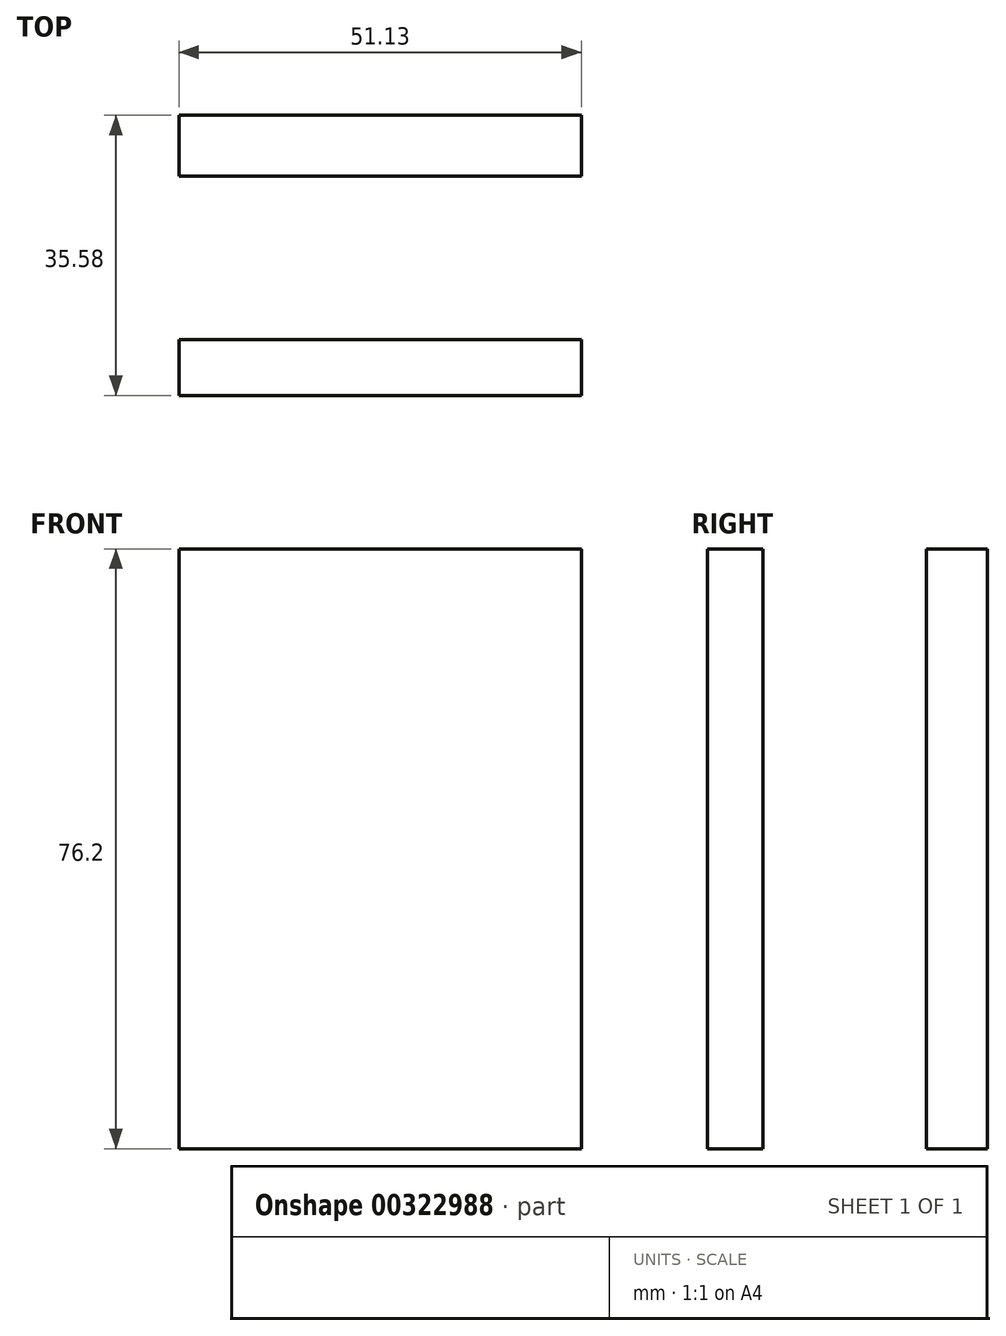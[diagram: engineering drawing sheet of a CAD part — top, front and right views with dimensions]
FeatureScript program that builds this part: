
annotation { "Feature Type Name" : "Feature", "Feature Type Description" : "" }
export const myFeature = defineFeature(function(context is Context, id is Id, definition is map)
    precondition{}
    {
        {
            var Q0;
            Q0=qCreatedBy(makeId("Top.planeOp"),FACE);
            var sketch = newSketch(context, id + "F0", { "sketchPlane" : qUnion([Q0])});
            skLineSegment(sketch, "E0", {"start": v(-59.97, 0) * mm, "end": v(-59.97, 35.58) * mm});
            skLineSegment(sketch, "E1", {"start": v(-59.97, 35.58) * mm, "end": v(-8.84, 35.58) * mm});
            skLineSegment(sketch, "E2", {"start": v(-8.84, 35.58) * mm, "end": v(-8.84, 0) * mm});
            skLineSegment(sketch, "E3", {"start": v(-8.84, 0) * mm, "end": v(-59.97, 0) * mm});
            skLineSegment(sketch, "E4", {"start": v(-59.97, 7.06) * mm, "end": v(-8.84, 7.06) * mm});
            skLineSegment(sketch, "E5", {"start": v(-8.84, 7.06) * mm, "end": v(-8.84, 27.83) * mm});
            skLineSegment(sketch, "E6", {"start": v(-8.84, 27.83) * mm, "end": v(-59.97, 27.83) * mm});
            skSolve(sketch);
        }
        {
            var Q0;
            {var subQ0=sQuery(id+"F0.wireOp",EDGE,"E3");Q0=makeQuery(id+"F0.imprint","IMPRINT",FACE,{"disambiguationData":[TD([[makeQuery(id+"F0.imprint","IMPRINT",EDGE,{"derivedFrom":subQ0}),-1.0]])]});}
            var Q1;
            {var subQ0=sQuery(id+"F0.wireOp",EDGE,"E1");Q1=makeQuery(id+"F0.imprint","IMPRINT",FACE,{"disambiguationData":[TD([[makeQuery(id+"F0.imprint","IMPRINT",EDGE,{"derivedFrom":subQ0}),-1.0]])]});}
            extrude(context, id + "F1", {"entities" : qUnion([Q0, Q1]), "depth" : 76.2 * mm});
        }
    });
